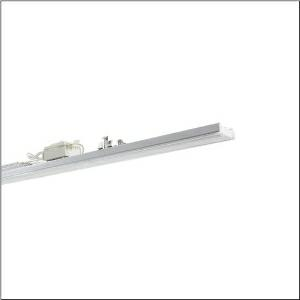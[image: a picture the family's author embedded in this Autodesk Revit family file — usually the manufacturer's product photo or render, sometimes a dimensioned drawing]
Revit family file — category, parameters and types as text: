
# Revit family: licross_21_recessed_mo_52tl1edn495g
name_source: partatom
category: Lighting Fixtures
units: mm (PartAtom-declared; Revit-internal decimal feet)

## family parameters
Cut with Voids When Loaded = No
Host = Face
Light Source = No
Part Type = Normal
Room Calculation Point = No
Round Connector Dimension = Use Diameter
Shared = No

## types (1)
- --- (1 x LED, 9940 lm, 58 W, 4000K)
    Apparent Load = 58 VA
    CIE Flux Codes = 85 95 99 100 100
    Color Rendering = 80
    Color Temperature = 4000K
    Default Elevation = 1800 mm
    Description = Licross 21 Recessed MO, luminaire insert, of sheet steel, galvanised, coil coated, white, length: 1.500mm, width: 66mm, height: 67mm, LED rated luminous flux: 9.940lm, light colour: 840, SDCM (Standard Deviation of Colour Matching)MacAdam ≤ 3 SDCM (initial), control gear: DALI 2, with plug, 5-pole, with phase selection, mains connection: 220..240V, AC, 50/60Hz, rated input power: 58W, internal wiring halogen-free, primary light control with lens, of plastic, primary optical cover: cover, of PMMA, light emission: direct distribution, primary light characteristic: symmetric, protection rating (complete): IP40, insulation class (complete): insulation class I (protective earthing), certification: CE, ENEC, VDE, UKCA, protection symbol: D if used in an environment without relevant dust loads with corresponding accessories, impact resistance: IK06, permissible ambient temperature for indoor applications: -25..+35°C, corresponds to IFS (International Featured Standards) requirements for safety and quality in the food industry, reducing of maximum allowable ambient temperature of 5°C with ceiling mounting, LABS conformity tested according to VDMA 24364:2018-05, The light source and the operating device comply with the requirements of the Ecodesign Regulation (EU) 2019/2020 and are replaceable in accordance with this regulation, packaging unit: 1 piece
    Height = 58 mm
    Lamp = 1 x LED
    Lamp Light Flux = 9940 lm
    Lamp Power = 58 W
    Lamp count = 1
    Length = 1500 mm
    Luminous efficacy = 171 lm/W
    Manufacturer = Siteco
    ModVariant = No
    Model = 52TL1EDN495G
    Mounting Place = Ceiling
    Mounting Type = Pendant
    Number of Poles = 1
    OnlyDefault = Yes
    Power Factor = 1
    Product Name = Licross 21 Recessed MO
    Product group = luminaire insert | ceiling pendant
    ProductGroupID = 901
    Protection Class = Protection class I
    Protection Degree = IP 40
    RLX_Detail_Level = 1
    RLX_Emergency_Light_Flux = 0 lm
    RLX_Emergency_Type = 0
    RLX_Emergency_Type_DB = No
    RlxData = <blob elided: 24921 chars, md5=fb0d3d02>
    Socket = socket
    Standby Power = 0 W
    System Light Flux = 9940 lm
    System Power = 58 W
    Type Comments = factory setting: luminous flux: 100 % | dim-lin: 254 | 390 mA
    Type Image = l_1296930.jpg
    URL = http://relux.com
    VarID = @adj_125387
    Voltage = 0 V
    Weight = 0.00 kg
    Width = 66 mm

## geometry (parser evidence)
native form markers: Blend x4, Sweep x9
no freeform markers — native parametric forms only
